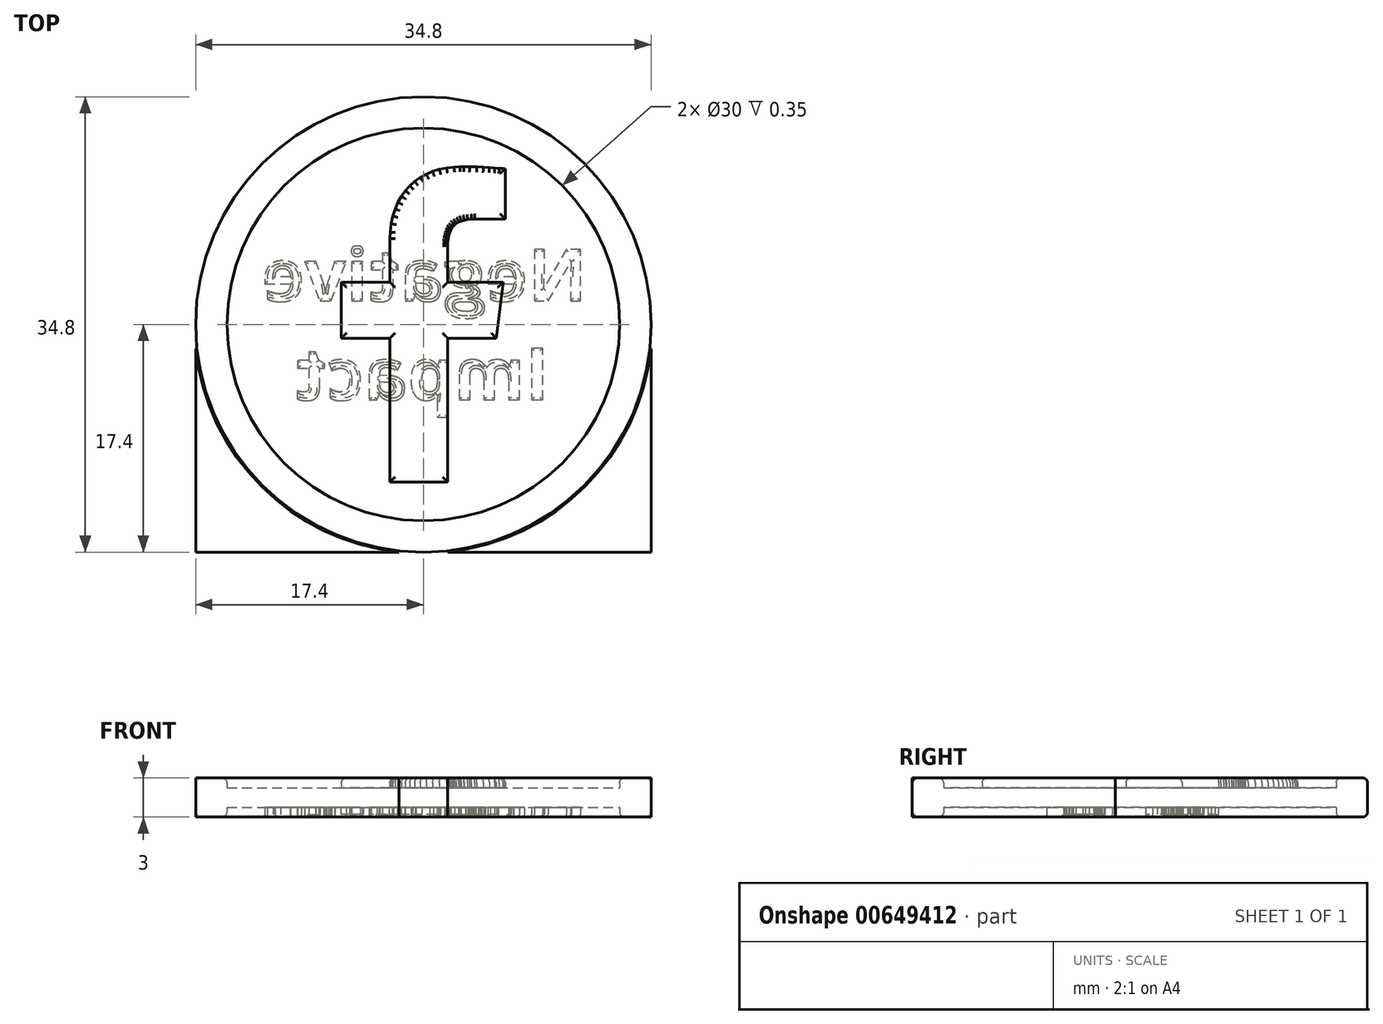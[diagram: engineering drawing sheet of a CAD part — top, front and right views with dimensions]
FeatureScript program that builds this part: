
annotation { "Feature Type Name" : "Feature", "Feature Type Description" : "" }
export const myFeature = defineFeature(function(context is Context, id is Id, definition is map)
    precondition{}
    {
        {
            var Q0;
            Q0=qCreatedBy(makeId("Front.planeOp"),FACE);
            var sketch = newSketch(context, id + "F0", { "sketchPlane" : qUnion([Q0])});
            skLineSegment(sketch, "E0", {"start": v(0, 0) * mm, "end": v(0, 0.75) * mm});
            skLineSegment(sketch, "E1", {"start": v(0, 0.75) * mm, "end": v(-15, 0.75) * mm});
            skLineSegment(sketch, "E2", {"start": v(-15, 0.75) * mm, "end": v(-17.4, 0.75) * mm});
            skLineSegment(sketch, "E3", {"start": v(-17.4, 0.75) * mm, "end": v(-17.4, 0) * mm});
            skLineSegment(sketch, "E4", {"start": v(-17.4, 0) * mm, "end": v(0, 0) * mm});
            skLineSegment(sketch, "E5", {"start": v(-15, 0.75) * mm, "end": v(-15, 0) * mm});
            skLineSegment(sketch, "E6.MirrorCS", {"start": v(0, 0) * mm, "end": v(0, -0.75) * mm});
            skLineSegment(sketch, "E7.MirrorCS", {"start": v(-15, -0.75) * mm, "end": v(-15, 0) * mm});
            skLineSegment(sketch, "E8.MirrorCS", {"start": v(-17.4, -0.75) * mm, "end": v(-17.4, 0) * mm});
            skLineSegment(sketch, "E9.MirrorCS", {"start": v(0, -0.75) * mm, "end": v(-15, -0.75) * mm});
            skLineSegment(sketch, "E10.MirrorCS", {"start": v(-15, -0.75) * mm, "end": v(-17.4, -0.75) * mm});
            skSolve(sketch);
        }
        {
            var Q0;
            {var subQ2=sQuery(id+"F0.wireOp",EDGE,"E7.MirrorCS");Q0=makeQuery(id+"F0.imprint","IMPRINT",FACE,{"disambiguationData":[TD([[makeQuery(id+"F0.imprint","IMPRINT",EDGE,{"derivedFrom":subQ2}),1.0]])]});}
            var Q1;
            Q1=makeQuery(id+"F0.imprint","IMPRINT",FACE,{"disambiguationData":[TD([[makeQuery(id+"F0.imprint","IMPRINT",EDGE,{"derivedFrom":sQuery(id+"F0.wireOp",EDGE,"E2")}),1.0]])]});
            var Q2;
            Q2=sQuery(id+"F0.wireOp",EDGE,"E0");
            revolve(context, id + "F1", {"entities" : qUnion([Q0, Q1]), "axis" : qUnion([Q2]), "revolveType" : RevolveType.FULL});
        }
        {
            var Q0;
            {var subQ0=sQuery(id+"F0.wireOp",EDGE,"E0");Q0=makeQuery(id+"F0.imprint","IMPRINT",FACE,{"disambiguationData":[TD([[makeQuery(id+"F0.imprint","IMPRINT",EDGE,{"derivedFrom":subQ0}),1.0]])]});}
            var Q1;
            {var subQ0=sQuery(id+"F0.wireOp",EDGE,"E6.MirrorCS");Q1=makeQuery(id+"F0.imprint","IMPRINT",FACE,{"disambiguationData":[TD([[makeQuery(id+"F0.imprint","IMPRINT",EDGE,{"derivedFrom":subQ0}),-1.0]])]});}
            var Q2;
            Q2=sQuery(id+"F0.wireOp",EDGE,"E0");
            revolve(context, id + "F2", {"entities" : qUnion([Q0, Q1]), "axis" : qUnion([Q2]), "revolveType" : RevolveType.FULL});
        }
        {
            var Q0;
            Q0=makeQuery(id+"F2.opRevolve","SWEPT_FACE",FACE,{"disambiguationData":[OSD([sQuery(id+"F0.wireOp",EDGE,"E1")])]});
            var sketch = newSketch(context, id + "F3", { "sketchPlane" : qUnion([Q0])});
            skLineSegment(sketch, "E11", {"start": v(1.87, -12.06) * mm, "end": v(1.87, -1.06) * mm});
            skLineSegment(sketch, "E12", {"start": v(1.87, -1.06) * mm, "end": v(5.56, -1.06) * mm});
            skLineSegment(sketch, "E13", {"start": v(5.56, -1.06) * mm, "end": v(6.11, 3.23) * mm});
            skLineSegment(sketch, "E14", {"start": v(6.11, 3.23) * mm, "end": v(1.87, 3.23) * mm});
            skLineSegment(sketch, "E15", {"start": v(1.87, 3.23) * mm, "end": v(1.87, 5.97) * mm});
            skLineSegment(sketch, "E16", {"start": v(1.87, 5.97) * mm, "end": v(1.87, 6.02) * mm});
            skLineSegment(sketch, "E17", {"start": v(1.87, 6.02) * mm, "end": v(1.87, 6.2) * mm});
            skLineSegment(sketch, "E18", {"start": v(1.87, 6.2) * mm, "end": v(1.89, 6.41) * mm});
            skLineSegment(sketch, "E19", {"start": v(1.89, 6.41) * mm, "end": v(1.91, 6.62) * mm});
            skLineSegment(sketch, "E20", {"start": v(1.91, 6.62) * mm, "end": v(1.95, 6.82) * mm});
            skLineSegment(sketch, "E21", {"start": v(1.95, 6.82) * mm, "end": v(2, 7) * mm});
            skLineSegment(sketch, "E22", {"start": v(2, 7) * mm, "end": v(2.07, 7.17) * mm});
            skLineSegment(sketch, "E23", {"start": v(2.07, 7.17) * mm, "end": v(2.16, 7.33) * mm});
            skLineSegment(sketch, "E24", {"start": v(2.16, 7.33) * mm, "end": v(2.26, 7.48) * mm});
            skLineSegment(sketch, "E25", {"start": v(2.26, 7.48) * mm, "end": v(2.39, 7.6) * mm});
            skLineSegment(sketch, "E26", {"start": v(2.39, 7.6) * mm, "end": v(2.54, 7.72) * mm});
            skLineSegment(sketch, "E27", {"start": v(2.54, 7.72) * mm, "end": v(2.71, 7.82) * mm});
            skLineSegment(sketch, "E28", {"start": v(2.71, 7.82) * mm, "end": v(2.9, 7.9) * mm});
            skLineSegment(sketch, "E29", {"start": v(2.9, 7.9) * mm, "end": v(3.13, 7.97) * mm});
            skLineSegment(sketch, "E30", {"start": v(3.13, 7.97) * mm, "end": v(3.39, 8.01) * mm});
            skLineSegment(sketch, "E31", {"start": v(3.39, 8.01) * mm, "end": v(3.67, 8.04) * mm});
            skLineSegment(sketch, "E32", {"start": v(3.67, 8.04) * mm, "end": v(3.91, 8.05) * mm});
            skLineSegment(sketch, "E33", {"start": v(3.91, 8.05) * mm, "end": v(4, 8.05) * mm});
            skLineSegment(sketch, "E34", {"start": v(4, 8.05) * mm, "end": v(6.26, 8.05) * mm});
            skLineSegment(sketch, "E35", {"start": v(6.26, 8.05) * mm, "end": v(6.26, 11.89) * mm});
            skLineSegment(sketch, "E36", {"start": v(6.26, 11.89) * mm, "end": v(6.21, 11.9) * mm});
            skLineSegment(sketch, "E37", {"start": v(6.21, 11.9) * mm, "end": v(6.07, 11.91) * mm});
            skLineSegment(sketch, "E38", {"start": v(6.07, 11.91) * mm, "end": v(5.8, 11.94) * mm});
            skLineSegment(sketch, "E39", {"start": v(5.8, 11.94) * mm, "end": v(5.46, 11.96) * mm});
            skLineSegment(sketch, "E40", {"start": v(5.46, 11.96) * mm, "end": v(5.05, 12) * mm});
            skLineSegment(sketch, "E41", {"start": v(5.05, 12) * mm, "end": v(4.59, 12.02) * mm});
            skLineSegment(sketch, "E42", {"start": v(4.59, 12.02) * mm, "end": v(4.08, 12.04) * mm});
            skLineSegment(sketch, "E43", {"start": v(4.08, 12.04) * mm, "end": v(3.53, 12.05) * mm});
            skLineSegment(sketch, "E44", {"start": v(3.53, 12.05) * mm, "end": v(3.1, 12.06) * mm});
            skLineSegment(sketch, "E45", {"start": v(3.1, 12.06) * mm, "end": v(2.95, 12.06) * mm});
            skLineSegment(sketch, "E46", {"start": v(2.95, 12.06) * mm, "end": v(2.8, 12.06) * mm});
            skLineSegment(sketch, "E47", {"start": v(2.8, 12.06) * mm, "end": v(2.35, 12.03) * mm});
            skLineSegment(sketch, "E48", {"start": v(2.35, 12.03) * mm, "end": v(1.78, 11.96) * mm});
            skLineSegment(sketch, "E49", {"start": v(1.78, 11.96) * mm, "end": v(1.23, 11.85) * mm});
            skLineSegment(sketch, "E50", {"start": v(1.23, 11.85) * mm, "end": v(0.71, 11.69) * mm});
            skLineSegment(sketch, "E51", {"start": v(0.71, 11.69) * mm, "end": v(0.22, 11.48) * mm});
            skLineSegment(sketch, "E52", {"start": v(0.22, 11.48) * mm, "end": v(-0.23, 11.23) * mm});
            skLineSegment(sketch, "E53", {"start": v(-0.23, 11.23) * mm, "end": v(-0.65, 10.94) * mm});
            skLineSegment(sketch, "E54", {"start": v(-0.65, 10.94) * mm, "end": v(-1.03, 10.6) * mm});
            skLineSegment(sketch, "E55", {"start": v(-1.03, 10.6) * mm, "end": v(-1.37, 10.22) * mm});
            skLineSegment(sketch, "E56", {"start": v(-1.37, 10.22) * mm, "end": v(-1.68, 9.8) * mm});
            skLineSegment(sketch, "E57", {"start": v(-1.68, 9.8) * mm, "end": v(-1.94, 9.33) * mm});
            skLineSegment(sketch, "E58", {"start": v(-1.94, 9.33) * mm, "end": v(-2.16, 8.82) * mm});
            skLineSegment(sketch, "E59", {"start": v(-2.16, 8.82) * mm, "end": v(-2.33, 8.28) * mm});
            skLineSegment(sketch, "E60", {"start": v(-2.33, 8.28) * mm, "end": v(-2.46, 7.69) * mm});
            skLineSegment(sketch, "E61", {"start": v(-2.46, 7.69) * mm, "end": v(-2.53, 7.06) * mm});
            skLineSegment(sketch, "E62", {"start": v(-2.53, 7.06) * mm, "end": v(-2.56, 6.56) * mm});
            skLineSegment(sketch, "E63", {"start": v(-2.56, 6.56) * mm, "end": v(-2.56, 6.4) * mm});
            skLineSegment(sketch, "E64", {"start": v(-2.56, 6.4) * mm, "end": v(-2.56, 3.23) * mm});
            skLineSegment(sketch, "E65", {"start": v(-2.56, 3.23) * mm, "end": v(-6.26, 3.23) * mm});
            skLineSegment(sketch, "E66", {"start": v(-6.26, 3.23) * mm, "end": v(-6.26, -1.06) * mm});
            skLineSegment(sketch, "E67", {"start": v(-6.26, -1.06) * mm, "end": v(-2.56, -1.06) * mm});
            skLineSegment(sketch, "E68", {"start": v(-2.56, -1.06) * mm, "end": v(-2.56, -12.06) * mm});
            skLineSegment(sketch, "E69", {"start": v(-2.56, -12.06) * mm, "end": v(1.87, -12.06) * mm});
            skSolve(sketch);
        }
        {
            var Q0;
            Q0=makeQuery(id+"F2.opRevolve","SWEPT_FACE",FACE,{"disambiguationData":[OSD([sQuery(id+"F0.wireOp",EDGE,"E9.MirrorCS")])]});
            var sketch = newSketch(context, id + "F4", { "sketchPlane" : qUnion([Q0])});
            skText(sketch, "E70", { "text": "Negative\n  Impact", "fontName": "OpenSans-Bold.ttf"});
            const initialGuessF4  = {"E70": [0.0125, -0.00178, -1, 0, 0.004]};
            skSetInitialGuess(sketch, initialGuessF4);
            skSolve(sketch);
        }
        {
            var Q0;
            Q0=makeQuery(id+"F3.imprint","IMPRINT",FACE,{"disambiguationData":[TD([[makeQuery(id+"F3.imprint","IMPRINT",EDGE,{"derivedFrom":sQuery(id+"F3.wireOp",EDGE,"E11")}),1.0]])]});
            var Q1;
            Q1=makeQuery(id+"F1.opRevolve","SWEPT_FACE",FACE,{"disambiguationData":[OSD([sQuery(id+"F0.wireOp",EDGE,"E2")])]});
            var Q2;
            Q2=makeQuery(id+"F1.opRevolve","SWEPT_FACE",FACE,{"disambiguationData":[OSD([sQuery(id+"F0.wireOp",EDGE,"E10.MirrorCS")])]});
            var Q3;
            Q3=makeQuery(id+"F4.imprint","IMPRINT",FACE,{"disambiguationData":[TD([[makeQuery(id+"F4.imprint","IMPRINT",EDGE,{"derivedFrom":sQuery(id+"F4.wireOp",EDGE,"e00e6bc2-6b43-4169-90cf-6a860700e017")}),1.0]])]});
            var Q4;
            Q4=makeQuery(id+"F4.imprint","IMPRINT",FACE,{"disambiguationData":[TD([[makeQuery(id+"F4.imprint","IMPRINT",EDGE,{"derivedFrom":sQuery(id+"F4.wireOp",EDGE,"cbd16ef6-c500-4ed5-8440-1c0017b8261a")}),-1.0]])]});
            var Q5;
            Q5=makeQuery(id+"F4.imprint","IMPRINT",FACE,{"disambiguationData":[TD([[makeQuery(id+"F4.imprint","IMPRINT",EDGE,{"derivedFrom":sQuery(id+"F4.wireOp",EDGE,"E70.sketch_text.stroke-34")}),-1.0]])]});
            var Q6;
            Q6=makeQuery(id+"F4.imprint","IMPRINT",FACE,{"disambiguationData":[TD([[makeQuery(id+"F4.imprint","IMPRINT",EDGE,{"derivedFrom":sQuery(id+"F4.wireOp",EDGE,"E70.sketch_text.stroke-14")}),-1.0]])]});
            var Q7;
            Q7=makeQuery(id+"F4.imprint","IMPRINT",FACE,{"disambiguationData":[TD([[makeQuery(id+"F4.imprint","IMPRINT",EDGE,{"derivedFrom":sQuery(id+"F4.wireOp",EDGE,"E70.sketch_text.stroke-0")}),-1.0]])]});
            var Q8;
            Q8=makeQuery(id+"F4.imprint","IMPRINT",FACE,{"disambiguationData":[TD([[makeQuery(id+"F4.imprint","IMPRINT",EDGE,{"derivedFrom":sQuery(id+"F4.wireOp",EDGE,"E70.sketch_text.stroke-160")}),-1.0]])]});
            var Q9;
            Q9=makeQuery(id+"F4.imprint","IMPRINT",FACE,{"disambiguationData":[TD([[makeQuery(id+"F4.imprint","IMPRINT",EDGE,{"derivedFrom":sQuery(id+"F4.wireOp",EDGE,"E70.sketch_text.stroke-164")}),-1.0]])]});
            var Q10;
            Q10=makeQuery(id+"F4.imprint","IMPRINT",FACE,{"disambiguationData":[TD([[makeQuery(id+"F4.imprint","IMPRINT",EDGE,{"derivedFrom":sQuery(id+"F4.wireOp",EDGE,"E70.sketch_text.stroke-192")}),-1.0]])]});
            var Q11;
            Q11=makeQuery(id+"F4.imprint","IMPRINT",FACE,{"disambiguationData":[TD([[makeQuery(id+"F4.imprint","IMPRINT",EDGE,{"derivedFrom":sQuery(id+"F4.wireOp",EDGE,"E70.sketch_text.stroke-215")}),-1.0]])]});
            var Q12;
            Q12=makeQuery(id+"F4.imprint","IMPRINT",FACE,{"disambiguationData":[TD([[makeQuery(id+"F4.imprint","IMPRINT",EDGE,{"derivedFrom":sQuery(id+"F4.wireOp",EDGE,"E70.sketch_text.stroke-240")}),-1.0]])]});
            var Q13;
            Q13=makeQuery(id+"F4.imprint","IMPRINT",FACE,{"disambiguationData":[TD([[makeQuery(id+"F4.imprint","IMPRINT",EDGE,{"derivedFrom":sQuery(id+"F4.wireOp",EDGE,"E70.sketch_text.stroke-254")}),-1.0]])]});
            var Q14;
            Q14=makeQuery(id+"F4.imprint","IMPRINT",FACE,{"disambiguationData":[TD([[makeQuery(id+"F4.imprint","IMPRINT",EDGE,{"derivedFrom":sQuery(id+"F4.wireOp",EDGE,"E70.sketch_text.stroke-78")}),-1.0]])]});
            var Q15;
            Q15=makeQuery(id+"F4.imprint","IMPRINT",FACE,{"disambiguationData":[TD([[makeQuery(id+"F4.imprint","IMPRINT",EDGE,{"derivedFrom":sQuery(id+"F4.wireOp",EDGE,"E70.sketch_text.stroke-103")}),-1.0]])]});
            var Q16;
            Q16=makeQuery(id+"F4.imprint","IMPRINT",FACE,{"disambiguationData":[TD([[makeQuery(id+"F4.imprint","IMPRINT",EDGE,{"derivedFrom":sQuery(id+"F4.wireOp",EDGE,"E70.sketch_text.stroke-126")}),-1.0]])]});
            var Q17;
            Q17=makeQuery(id+"F4.imprint","IMPRINT",FACE,{"disambiguationData":[TD([[makeQuery(id+"F4.imprint","IMPRINT",EDGE,{"derivedFrom":sQuery(id+"F4.wireOp",EDGE,"E70.sketch_text.stroke-121")}),-1.0]])]});
            var Q18;
            Q18=makeQuery(id+"F4.imprint","IMPRINT",FACE,{"disambiguationData":[TD([[makeQuery(id+"F4.imprint","IMPRINT",EDGE,{"derivedFrom":sQuery(id+"F4.wireOp",EDGE,"E70.sketch_text.stroke-130")}),-1.0]])]});
            var Q19;
            Q19=makeQuery(id+"F4.imprint","IMPRINT",FACE,{"disambiguationData":[TD([[makeQuery(id+"F4.imprint","IMPRINT",EDGE,{"derivedFrom":sQuery(id+"F4.wireOp",EDGE,"E70.sketch_text.stroke-140")}),-1.0]])]});
            extrude(context, id + "F5", {"entities" : qUnion([Q0, Q1, Q2, Q3, Q4, Q5, Q6, Q7, Q8, Q9, Q10, Q11, Q12, Q13, Q14, Q15, Q16, Q17, Q18, Q19]), "operationType" : NewBodyOperationType.ADD, "endBound" : BoundingType.SYMMETRIC, "depth" : 1.5 * mm, "offsetDistance" : 25 * mm});
        }
        {
            var Q0;
            Q0=makeQuery(id+"F5.opExtrude","CAP_FACE",FACE,{"disambiguationData":[OSD([sQuery(id+"F0.wireOp",EDGE,"E10.MirrorCS")])],"isStart":true});
            var Q1;
            Q1=makeQuery(id+"F5.opExtrude","CAP_FACE",FACE,{"disambiguationData":[OSD([sQuery(id+"F0.wireOp",EDGE,"E2")])],"isStart":false});
            var Q2;
            Q2=makeQuery(id+"F5.opExtrude","CAP_FACE",FACE,{"disambiguationData":[OSD([sQuery(id+"F4.wireOp",EDGE,"cbd16ef6-c500-4ed5-8440-1c0017b8261a"),sQuery(id+"F4.wireOp",EDGE,"0d944bf3-0ec5-4c38-9916-8d3f37ee8ac4"),sQuery(id+"F4.wireOp",EDGE,"81174dc4-763a-49ac-b099-c01943fa321f"),sQuery(id+"F4.wireOp",EDGE,"576b59ee-5a98-45c4-9437-15f9f7d92798"),sQuery(id+"F4.wireOp",EDGE,"b6bc0b02-f75e-45d8-90bf-1eabf7058279"),sQuery(id+"F4.wireOp",EDGE,"73b536a1-ebc0-4c82-85a4-445a789f644d"),sQuery(id+"F4.wireOp",EDGE,"f7087b31-3228-4bf9-8aa5-93d670d5cce0"),sQuery(id+"F4.wireOp",EDGE,"741630d7-2485-4888-9f90-699ab1dbe6b0"),sQuery(id+"F4.wireOp",EDGE,"e8cdc173-4411-4f79-96bc-056ef1efb820"),sQuery(id+"F4.wireOp",EDGE,"f2d56595-1831-41da-a059-6a4e7aeb48ed"),sQuery(id+"F4.wireOp",EDGE,"39ab4d4d-5ef3-4ee6-bd97-17733d594e21"),sQuery(id+"F4.wireOp",EDGE,"2d56eba7-b366-4cc2-9c15-0fc1e6917ac3"),sQuery(id+"F4.wireOp",EDGE,"xFnOpOKS-PgkY-Xr0f-Dgug-B9nhrKbz7dnA"),sQuery(id+"F4.wireOp",EDGE,"wusehGa3-lIWQ-oOtp-HWoc-AapjoZAoam0S")])],"isStart":true});
            var Q3;
            Q3=makeQuery(id+"F5.opExtrude","CAP_FACE",FACE,{"disambiguationData":[OSD([sQuery(id+"F4.wireOp",EDGE,"e00e6bc2-6b43-4169-90cf-6a860700e017")])],"isStart":true});
            var Q4;
            Q4=makeQuery(id+"F5.opExtrude","CAP_FACE",FACE,{"disambiguationData":[OSD([sQuery(id+"F3.wireOp",EDGE,"E11"),sQuery(id+"F3.wireOp",EDGE,"E12"),sQuery(id+"F3.wireOp",EDGE,"E13"),sQuery(id+"F3.wireOp",EDGE,"E14"),sQuery(id+"F3.wireOp",EDGE,"E15"),sQuery(id+"F3.wireOp",EDGE,"E16"),sQuery(id+"F3.wireOp",EDGE,"E17"),sQuery(id+"F3.wireOp",EDGE,"E18"),sQuery(id+"F3.wireOp",EDGE,"E19"),sQuery(id+"F3.wireOp",EDGE,"E20"),sQuery(id+"F3.wireOp",EDGE,"E21"),sQuery(id+"F3.wireOp",EDGE,"E22"),sQuery(id+"F3.wireOp",EDGE,"E23"),sQuery(id+"F3.wireOp",EDGE,"E24"),sQuery(id+"F3.wireOp",EDGE,"E25"),sQuery(id+"F3.wireOp",EDGE,"E26"),sQuery(id+"F3.wireOp",EDGE,"E27"),sQuery(id+"F3.wireOp",EDGE,"E28"),sQuery(id+"F3.wireOp",EDGE,"E29"),sQuery(id+"F3.wireOp",EDGE,"E30"),sQuery(id+"F3.wireOp",EDGE,"E31"),sQuery(id+"F3.wireOp",EDGE,"E32"),sQuery(id+"F3.wireOp",EDGE,"E33"),sQuery(id+"F3.wireOp",EDGE,"E34"),sQuery(id+"F3.wireOp",EDGE,"E35"),sQuery(id+"F3.wireOp",EDGE,"E36"),sQuery(id+"F3.wireOp",EDGE,"E37"),sQuery(id+"F3.wireOp",EDGE,"E38"),sQuery(id+"F3.wireOp",EDGE,"E39"),sQuery(id+"F3.wireOp",EDGE,"E40"),sQuery(id+"F3.wireOp",EDGE,"E41"),sQuery(id+"F3.wireOp",EDGE,"E42"),sQuery(id+"F3.wireOp",EDGE,"E43"),sQuery(id+"F3.wireOp",EDGE,"E44"),sQuery(id+"F3.wireOp",EDGE,"E45"),sQuery(id+"F3.wireOp",EDGE,"E46"),sQuery(id+"F3.wireOp",EDGE,"E47"),sQuery(id+"F3.wireOp",EDGE,"E48"),sQuery(id+"F3.wireOp",EDGE,"E49"),sQuery(id+"F3.wireOp",EDGE,"E50"),sQuery(id+"F3.wireOp",EDGE,"E51"),sQuery(id+"F3.wireOp",EDGE,"E52"),sQuery(id+"F3.wireOp",EDGE,"E53"),sQuery(id+"F3.wireOp",EDGE,"E54"),sQuery(id+"F3.wireOp",EDGE,"E55"),sQuery(id+"F3.wireOp",EDGE,"E56"),sQuery(id+"F3.wireOp",EDGE,"E57"),sQuery(id+"F3.wireOp",EDGE,"E58"),sQuery(id+"F3.wireOp",EDGE,"E59"),sQuery(id+"F3.wireOp",EDGE,"E60"),sQuery(id+"F3.wireOp",EDGE,"E61"),sQuery(id+"F3.wireOp",EDGE,"E62"),sQuery(id+"F3.wireOp",EDGE,"E63"),sQuery(id+"F3.wireOp",EDGE,"E64"),sQuery(id+"F3.wireOp",EDGE,"E65"),sQuery(id+"F3.wireOp",EDGE,"E66"),sQuery(id+"F3.wireOp",EDGE,"E67"),sQuery(id+"F3.wireOp",EDGE,"E68"),sQuery(id+"F3.wireOp",EDGE,"E69")])],"isStart":false});
            fillet(context, id + "F6", {"entities" : qUnion([Q0, Q1, Q2, Q3, Q4]), "radius" : 0.4 * mm, "tangentPropagation" : true, "allowEdgeOverflow" : false});
        }
        {
            var Q0;
            Q0=makeQuery(id+"F5.opExtrude","CAP_FACE",FACE,{"disambiguationData":[OSD([sQuery(id+"F4.wireOp",EDGE,"E70.sketch_text.stroke-0"),sQuery(id+"F4.wireOp",EDGE,"E70.sketch_text.stroke-1"),sQuery(id+"F4.wireOp",EDGE,"E70.sketch_text.stroke-2"),sQuery(id+"F4.wireOp",EDGE,"E70.sketch_text.stroke-3"),sQuery(id+"F4.wireOp",EDGE,"E70.sketch_text.stroke-4"),sQuery(id+"F4.wireOp",EDGE,"E70.sketch_text.stroke-5"),sQuery(id+"F4.wireOp",EDGE,"E70.sketch_text.stroke-6"),sQuery(id+"F4.wireOp",EDGE,"E70.sketch_text.stroke-7"),sQuery(id+"F4.wireOp",EDGE,"E70.sketch_text.stroke-8"),sQuery(id+"F4.wireOp",EDGE,"E70.sketch_text.stroke-9"),sQuery(id+"F4.wireOp",EDGE,"E70.sketch_text.stroke-10"),sQuery(id+"F4.wireOp",EDGE,"E70.sketch_text.stroke-11"),sQuery(id+"F4.wireOp",EDGE,"E70.sketch_text.stroke-12"),sQuery(id+"F4.wireOp",EDGE,"E70.sketch_text.stroke-13")])],"isStart":true});
            var Q1;
            Q1=makeQuery(id+"F5.opExtrude","CAP_FACE",FACE,{"disambiguationData":[OSD([sQuery(id+"F4.wireOp",EDGE,"E70.sketch_text.stroke-14"),sQuery(id+"F4.wireOp",EDGE,"E70.sketch_text.stroke-15"),sQuery(id+"F4.wireOp",EDGE,"E70.sketch_text.stroke-16"),sQuery(id+"F4.wireOp",EDGE,"E70.sketch_text.stroke-17"),sQuery(id+"F4.wireOp",EDGE,"E70.sketch_text.stroke-18"),sQuery(id+"F4.wireOp",EDGE,"E70.sketch_text.stroke-19"),sQuery(id+"F4.wireOp",EDGE,"E70.sketch_text.stroke-20"),sQuery(id+"F4.wireOp",EDGE,"E70.sketch_text.stroke-21"),sQuery(id+"F4.wireOp",EDGE,"E70.sketch_text.stroke-22"),sQuery(id+"F4.wireOp",EDGE,"E70.sketch_text.stroke-23"),sQuery(id+"F4.wireOp",EDGE,"E70.sketch_text.stroke-24"),sQuery(id+"F4.wireOp",EDGE,"E70.sketch_text.stroke-25"),sQuery(id+"F4.wireOp",EDGE,"E70.sketch_text.stroke-26"),sQuery(id+"F4.wireOp",EDGE,"E70.sketch_text.stroke-27"),sQuery(id+"F4.wireOp",EDGE,"E70.sketch_text.stroke-28"),sQuery(id+"F4.wireOp",EDGE,"E70.sketch_text.stroke-29"),sQuery(id+"F4.wireOp",EDGE,"E70.sketch_text.stroke-30"),sQuery(id+"F4.wireOp",EDGE,"E70.sketch_text.stroke-31"),sQuery(id+"F4.wireOp",EDGE,"E70.sketch_text.stroke-32"),sQuery(id+"F4.wireOp",EDGE,"E70.sketch_text.stroke-33")])],"isStart":true});
            var Q2;
            Q2=makeQuery(id+"F5.opExtrude","CAP_FACE",FACE,{"disambiguationData":[OSD([sQuery(id+"F4.wireOp",EDGE,"E70.sketch_text.stroke-34"),sQuery(id+"F4.wireOp",EDGE,"E70.sketch_text.stroke-35"),sQuery(id+"F4.wireOp",EDGE,"E70.sketch_text.stroke-36"),sQuery(id+"F4.wireOp",EDGE,"E70.sketch_text.stroke-37"),sQuery(id+"F4.wireOp",EDGE,"E70.sketch_text.stroke-38"),sQuery(id+"F4.wireOp",EDGE,"E70.sketch_text.stroke-39"),sQuery(id+"F4.wireOp",EDGE,"E70.sketch_text.stroke-40"),sQuery(id+"F4.wireOp",EDGE,"E70.sketch_text.stroke-41"),sQuery(id+"F4.wireOp",EDGE,"E70.sketch_text.stroke-42"),sQuery(id+"F4.wireOp",EDGE,"E70.sketch_text.stroke-43"),sQuery(id+"F4.wireOp",EDGE,"E70.sketch_text.stroke-44"),sQuery(id+"F4.wireOp",EDGE,"E70.sketch_text.stroke-45"),sQuery(id+"F4.wireOp",EDGE,"E70.sketch_text.stroke-46"),sQuery(id+"F4.wireOp",EDGE,"E70.sketch_text.stroke-47"),sQuery(id+"F4.wireOp",EDGE,"E70.sketch_text.stroke-48"),sQuery(id+"F4.wireOp",EDGE,"E70.sketch_text.stroke-49"),sQuery(id+"F4.wireOp",EDGE,"E70.sketch_text.stroke-50"),sQuery(id+"F4.wireOp",EDGE,"E70.sketch_text.stroke-51"),sQuery(id+"F4.wireOp",EDGE,"E70.sketch_text.stroke-52"),sQuery(id+"F4.wireOp",EDGE,"E70.sketch_text.stroke-53"),sQuery(id+"F4.wireOp",EDGE,"E70.sketch_text.stroke-54"),sQuery(id+"F4.wireOp",EDGE,"E70.sketch_text.stroke-55"),sQuery(id+"F4.wireOp",EDGE,"E70.sketch_text.stroke-56"),sQuery(id+"F4.wireOp",EDGE,"E70.sketch_text.stroke-57"),sQuery(id+"F4.wireOp",EDGE,"E70.sketch_text.stroke-58"),sQuery(id+"F4.wireOp",EDGE,"E70.sketch_text.stroke-59"),sQuery(id+"F4.wireOp",EDGE,"E70.sketch_text.stroke-60"),sQuery(id+"F4.wireOp",EDGE,"E70.sketch_text.stroke-61"),sQuery(id+"F4.wireOp",EDGE,"E70.sketch_text.stroke-62"),sQuery(id+"F4.wireOp",EDGE,"E70.sketch_text.stroke-63"),sQuery(id+"F4.wireOp",EDGE,"E70.sketch_text.stroke-64"),sQuery(id+"F4.wireOp",EDGE,"E70.sketch_text.stroke-65"),sQuery(id+"F4.wireOp",EDGE,"E70.sketch_text.stroke-66"),sQuery(id+"F4.wireOp",EDGE,"E70.sketch_text.stroke-67"),sQuery(id+"F4.wireOp",EDGE,"E70.sketch_text.stroke-68"),sQuery(id+"F4.wireOp",EDGE,"E70.sketch_text.stroke-69"),sQuery(id+"F4.wireOp",EDGE,"E70.sketch_text.stroke-70"),sQuery(id+"F4.wireOp",EDGE,"E70.sketch_text.stroke-71"),sQuery(id+"F4.wireOp",EDGE,"E70.sketch_text.stroke-72"),sQuery(id+"F4.wireOp",EDGE,"E70.sketch_text.stroke-73"),sQuery(id+"F4.wireOp",EDGE,"E70.sketch_text.stroke-74"),sQuery(id+"F4.wireOp",EDGE,"E70.sketch_text.stroke-75"),sQuery(id+"F4.wireOp",EDGE,"E70.sketch_text.stroke-76"),sQuery(id+"F4.wireOp",EDGE,"E70.sketch_text.stroke-77")])],"isStart":true});
            var Q3;
            Q3=makeQuery(id+"F5.opExtrude","CAP_FACE",FACE,{"disambiguationData":[OSD([sQuery(id+"F4.wireOp",EDGE,"E70.sketch_text.stroke-78"),sQuery(id+"F4.wireOp",EDGE,"E70.sketch_text.stroke-79"),sQuery(id+"F4.wireOp",EDGE,"E70.sketch_text.stroke-80"),sQuery(id+"F4.wireOp",EDGE,"E70.sketch_text.stroke-81"),sQuery(id+"F4.wireOp",EDGE,"E70.sketch_text.stroke-82"),sQuery(id+"F4.wireOp",EDGE,"E70.sketch_text.stroke-83"),sQuery(id+"F4.wireOp",EDGE,"E70.sketch_text.stroke-84"),sQuery(id+"F4.wireOp",EDGE,"E70.sketch_text.stroke-85"),sQuery(id+"F4.wireOp",EDGE,"E70.sketch_text.stroke-86"),sQuery(id+"F4.wireOp",EDGE,"E70.sketch_text.stroke-87"),sQuery(id+"F4.wireOp",EDGE,"E70.sketch_text.stroke-88"),sQuery(id+"F4.wireOp",EDGE,"E70.sketch_text.stroke-89"),sQuery(id+"F4.wireOp",EDGE,"E70.sketch_text.stroke-90"),sQuery(id+"F4.wireOp",EDGE,"E70.sketch_text.stroke-91"),sQuery(id+"F4.wireOp",EDGE,"E70.sketch_text.stroke-92"),sQuery(id+"F4.wireOp",EDGE,"E70.sketch_text.stroke-93"),sQuery(id+"F4.wireOp",EDGE,"E70.sketch_text.stroke-94"),sQuery(id+"F4.wireOp",EDGE,"E70.sketch_text.stroke-95"),sQuery(id+"F4.wireOp",EDGE,"E70.sketch_text.stroke-96"),sQuery(id+"F4.wireOp",EDGE,"E70.sketch_text.stroke-97"),sQuery(id+"F4.wireOp",EDGE,"E70.sketch_text.stroke-98"),sQuery(id+"F4.wireOp",EDGE,"E70.sketch_text.stroke-99"),sQuery(id+"F4.wireOp",EDGE,"E70.sketch_text.stroke-100"),sQuery(id+"F4.wireOp",EDGE,"E70.sketch_text.stroke-101"),sQuery(id+"F4.wireOp",EDGE,"E70.sketch_text.stroke-102")])],"isStart":true});
            var Q4;
            Q4=makeQuery(id+"F5.opExtrude","CAP_FACE",FACE,{"disambiguationData":[OSD([sQuery(id+"F4.wireOp",EDGE,"E70.sketch_text.stroke-103"),sQuery(id+"F4.wireOp",EDGE,"E70.sketch_text.stroke-104"),sQuery(id+"F4.wireOp",EDGE,"E70.sketch_text.stroke-105"),sQuery(id+"F4.wireOp",EDGE,"E70.sketch_text.stroke-106"),sQuery(id+"F4.wireOp",EDGE,"E70.sketch_text.stroke-107"),sQuery(id+"F4.wireOp",EDGE,"E70.sketch_text.stroke-108"),sQuery(id+"F4.wireOp",EDGE,"E70.sketch_text.stroke-109"),sQuery(id+"F4.wireOp",EDGE,"E70.sketch_text.stroke-110"),sQuery(id+"F4.wireOp",EDGE,"E70.sketch_text.stroke-111"),sQuery(id+"F4.wireOp",EDGE,"E70.sketch_text.stroke-112"),sQuery(id+"F4.wireOp",EDGE,"E70.sketch_text.stroke-113"),sQuery(id+"F4.wireOp",EDGE,"E70.sketch_text.stroke-114"),sQuery(id+"F4.wireOp",EDGE,"E70.sketch_text.stroke-115"),sQuery(id+"F4.wireOp",EDGE,"E70.sketch_text.stroke-116"),sQuery(id+"F4.wireOp",EDGE,"E70.sketch_text.stroke-117"),sQuery(id+"F4.wireOp",EDGE,"E70.sketch_text.stroke-118"),sQuery(id+"F4.wireOp",EDGE,"E70.sketch_text.stroke-119"),sQuery(id+"F4.wireOp",EDGE,"E70.sketch_text.stroke-120")])],"isStart":true});
            var Q5;
            Q5=makeQuery(id+"F5.opExtrude","CAP_FACE",FACE,{"disambiguationData":[OSD([sQuery(id+"F4.wireOp",EDGE,"E70.sketch_text.stroke-126"),sQuery(id+"F4.wireOp",EDGE,"E70.sketch_text.stroke-127"),sQuery(id+"F4.wireOp",EDGE,"E70.sketch_text.stroke-128"),sQuery(id+"F4.wireOp",EDGE,"E70.sketch_text.stroke-129")])],"isStart":true});
            var Q6;
            Q6=makeQuery(id+"F5.opExtrude","CAP_FACE",FACE,{"disambiguationData":[OSD([sQuery(id+"F4.wireOp",EDGE,"E70.sketch_text.stroke-121"),sQuery(id+"F4.wireOp",EDGE,"E70.sketch_text.stroke-122"),sQuery(id+"F4.wireOp",EDGE,"E70.sketch_text.stroke-123"),sQuery(id+"F4.wireOp",EDGE,"E70.sketch_text.stroke-124"),sQuery(id+"F4.wireOp",EDGE,"E70.sketch_text.stroke-125")])],"isStart":true});
            var Q7;
            Q7=makeQuery(id+"F5.opExtrude","CAP_FACE",FACE,{"disambiguationData":[OSD([sQuery(id+"F4.wireOp",EDGE,"E70.sketch_text.stroke-130"),sQuery(id+"F4.wireOp",EDGE,"E70.sketch_text.stroke-131"),sQuery(id+"F4.wireOp",EDGE,"E70.sketch_text.stroke-132"),sQuery(id+"F4.wireOp",EDGE,"E70.sketch_text.stroke-133"),sQuery(id+"F4.wireOp",EDGE,"E70.sketch_text.stroke-134"),sQuery(id+"F4.wireOp",EDGE,"E70.sketch_text.stroke-135"),sQuery(id+"F4.wireOp",EDGE,"E70.sketch_text.stroke-136"),sQuery(id+"F4.wireOp",EDGE,"E70.sketch_text.stroke-137"),sQuery(id+"F4.wireOp",EDGE,"E70.sketch_text.stroke-138"),sQuery(id+"F4.wireOp",EDGE,"E70.sketch_text.stroke-139")])],"isStart":true});
            var Q8;
            Q8=makeQuery(id+"F5.opExtrude","CAP_FACE",FACE,{"disambiguationData":[OSD([sQuery(id+"F4.wireOp",EDGE,"E70.sketch_text.stroke-140"),sQuery(id+"F4.wireOp",EDGE,"E70.sketch_text.stroke-141"),sQuery(id+"F4.wireOp",EDGE,"E70.sketch_text.stroke-142"),sQuery(id+"F4.wireOp",EDGE,"E70.sketch_text.stroke-143"),sQuery(id+"F4.wireOp",EDGE,"E70.sketch_text.stroke-144"),sQuery(id+"F4.wireOp",EDGE,"E70.sketch_text.stroke-145"),sQuery(id+"F4.wireOp",EDGE,"E70.sketch_text.stroke-146"),sQuery(id+"F4.wireOp",EDGE,"E70.sketch_text.stroke-147"),sQuery(id+"F4.wireOp",EDGE,"E70.sketch_text.stroke-148"),sQuery(id+"F4.wireOp",EDGE,"E70.sketch_text.stroke-149"),sQuery(id+"F4.wireOp",EDGE,"E70.sketch_text.stroke-150"),sQuery(id+"F4.wireOp",EDGE,"E70.sketch_text.stroke-151"),sQuery(id+"F4.wireOp",EDGE,"E70.sketch_text.stroke-152"),sQuery(id+"F4.wireOp",EDGE,"E70.sketch_text.stroke-153"),sQuery(id+"F4.wireOp",EDGE,"E70.sketch_text.stroke-154"),sQuery(id+"F4.wireOp",EDGE,"E70.sketch_text.stroke-155"),sQuery(id+"F4.wireOp",EDGE,"E70.sketch_text.stroke-156"),sQuery(id+"F4.wireOp",EDGE,"E70.sketch_text.stroke-157"),sQuery(id+"F4.wireOp",EDGE,"E70.sketch_text.stroke-158"),sQuery(id+"F4.wireOp",EDGE,"E70.sketch_text.stroke-159")])],"isStart":true});
            var Q9;
            Q9=makeQuery(id+"F5.opExtrude","CAP_FACE",FACE,{"disambiguationData":[OSD([sQuery(id+"F4.wireOp",EDGE,"E70.sketch_text.stroke-160"),sQuery(id+"F4.wireOp",EDGE,"E70.sketch_text.stroke-161"),sQuery(id+"F4.wireOp",EDGE,"E70.sketch_text.stroke-162"),sQuery(id+"F4.wireOp",EDGE,"E70.sketch_text.stroke-163")])],"isStart":true});
            var Q10;
            Q10=makeQuery(id+"F5.opExtrude","CAP_FACE",FACE,{"disambiguationData":[OSD([sQuery(id+"F4.wireOp",EDGE,"E70.sketch_text.stroke-164"),sQuery(id+"F4.wireOp",EDGE,"E70.sketch_text.stroke-165"),sQuery(id+"F4.wireOp",EDGE,"E70.sketch_text.stroke-166"),sQuery(id+"F4.wireOp",EDGE,"E70.sketch_text.stroke-167"),sQuery(id+"F4.wireOp",EDGE,"E70.sketch_text.stroke-168"),sQuery(id+"F4.wireOp",EDGE,"E70.sketch_text.stroke-169"),sQuery(id+"F4.wireOp",EDGE,"E70.sketch_text.stroke-170"),sQuery(id+"F4.wireOp",EDGE,"E70.sketch_text.stroke-171"),sQuery(id+"F4.wireOp",EDGE,"E70.sketch_text.stroke-172"),sQuery(id+"F4.wireOp",EDGE,"E70.sketch_text.stroke-173"),sQuery(id+"F4.wireOp",EDGE,"E70.sketch_text.stroke-174"),sQuery(id+"F4.wireOp",EDGE,"E70.sketch_text.stroke-175"),sQuery(id+"F4.wireOp",EDGE,"E70.sketch_text.stroke-176"),sQuery(id+"F4.wireOp",EDGE,"E70.sketch_text.stroke-177"),sQuery(id+"F4.wireOp",EDGE,"E70.sketch_text.stroke-178"),sQuery(id+"F4.wireOp",EDGE,"E70.sketch_text.stroke-179"),sQuery(id+"F4.wireOp",EDGE,"E70.sketch_text.stroke-180"),sQuery(id+"F4.wireOp",EDGE,"E70.sketch_text.stroke-181"),sQuery(id+"F4.wireOp",EDGE,"E70.sketch_text.stroke-182"),sQuery(id+"F4.wireOp",EDGE,"E70.sketch_text.stroke-183"),sQuery(id+"F4.wireOp",EDGE,"E70.sketch_text.stroke-184"),sQuery(id+"F4.wireOp",EDGE,"E70.sketch_text.stroke-185"),sQuery(id+"F4.wireOp",EDGE,"E70.sketch_text.stroke-186"),sQuery(id+"F4.wireOp",EDGE,"E70.sketch_text.stroke-187"),sQuery(id+"F4.wireOp",EDGE,"E70.sketch_text.stroke-188"),sQuery(id+"F4.wireOp",EDGE,"E70.sketch_text.stroke-189"),sQuery(id+"F4.wireOp",EDGE,"E70.sketch_text.stroke-190"),sQuery(id+"F4.wireOp",EDGE,"E70.sketch_text.stroke-191")])],"isStart":true});
            var Q11;
            Q11=makeQuery(id+"F5.opExtrude","CAP_FACE",FACE,{"disambiguationData":[OSD([sQuery(id+"F4.wireOp",EDGE,"E70.sketch_text.stroke-192"),sQuery(id+"F4.wireOp",EDGE,"E70.sketch_text.stroke-193"),sQuery(id+"F4.wireOp",EDGE,"E70.sketch_text.stroke-194"),sQuery(id+"F4.wireOp",EDGE,"E70.sketch_text.stroke-195"),sQuery(id+"F4.wireOp",EDGE,"E70.sketch_text.stroke-196"),sQuery(id+"F4.wireOp",EDGE,"E70.sketch_text.stroke-197"),sQuery(id+"F4.wireOp",EDGE,"E70.sketch_text.stroke-198"),sQuery(id+"F4.wireOp",EDGE,"E70.sketch_text.stroke-199"),sQuery(id+"F4.wireOp",EDGE,"E70.sketch_text.stroke-200"),sQuery(id+"F4.wireOp",EDGE,"E70.sketch_text.stroke-201"),sQuery(id+"F4.wireOp",EDGE,"E70.sketch_text.stroke-202"),sQuery(id+"F4.wireOp",EDGE,"E70.sketch_text.stroke-203"),sQuery(id+"F4.wireOp",EDGE,"E70.sketch_text.stroke-204"),sQuery(id+"F4.wireOp",EDGE,"E70.sketch_text.stroke-205"),sQuery(id+"F4.wireOp",EDGE,"E70.sketch_text.stroke-206"),sQuery(id+"F4.wireOp",EDGE,"E70.sketch_text.stroke-207"),sQuery(id+"F4.wireOp",EDGE,"E70.sketch_text.stroke-208"),sQuery(id+"F4.wireOp",EDGE,"E70.sketch_text.stroke-209"),sQuery(id+"F4.wireOp",EDGE,"E70.sketch_text.stroke-210"),sQuery(id+"F4.wireOp",EDGE,"E70.sketch_text.stroke-211"),sQuery(id+"F4.wireOp",EDGE,"E70.sketch_text.stroke-212"),sQuery(id+"F4.wireOp",EDGE,"E70.sketch_text.stroke-213"),sQuery(id+"F4.wireOp",EDGE,"E70.sketch_text.stroke-214")])],"isStart":true});
            var Q12;
            Q12=makeQuery(id+"F5.opExtrude","CAP_FACE",FACE,{"disambiguationData":[OSD([sQuery(id+"F4.wireOp",EDGE,"E70.sketch_text.stroke-215"),sQuery(id+"F4.wireOp",EDGE,"E70.sketch_text.stroke-216"),sQuery(id+"F4.wireOp",EDGE,"E70.sketch_text.stroke-217"),sQuery(id+"F4.wireOp",EDGE,"E70.sketch_text.stroke-218"),sQuery(id+"F4.wireOp",EDGE,"E70.sketch_text.stroke-219"),sQuery(id+"F4.wireOp",EDGE,"E70.sketch_text.stroke-220"),sQuery(id+"F4.wireOp",EDGE,"E70.sketch_text.stroke-221"),sQuery(id+"F4.wireOp",EDGE,"E70.sketch_text.stroke-222"),sQuery(id+"F4.wireOp",EDGE,"E70.sketch_text.stroke-223"),sQuery(id+"F4.wireOp",EDGE,"E70.sketch_text.stroke-224"),sQuery(id+"F4.wireOp",EDGE,"E70.sketch_text.stroke-225"),sQuery(id+"F4.wireOp",EDGE,"E70.sketch_text.stroke-226"),sQuery(id+"F4.wireOp",EDGE,"E70.sketch_text.stroke-227"),sQuery(id+"F4.wireOp",EDGE,"E70.sketch_text.stroke-228"),sQuery(id+"F4.wireOp",EDGE,"E70.sketch_text.stroke-229"),sQuery(id+"F4.wireOp",EDGE,"E70.sketch_text.stroke-230"),sQuery(id+"F4.wireOp",EDGE,"E70.sketch_text.stroke-231"),sQuery(id+"F4.wireOp",EDGE,"E70.sketch_text.stroke-232"),sQuery(id+"F4.wireOp",EDGE,"E70.sketch_text.stroke-233"),sQuery(id+"F4.wireOp",EDGE,"E70.sketch_text.stroke-234"),sQuery(id+"F4.wireOp",EDGE,"E70.sketch_text.stroke-235"),sQuery(id+"F4.wireOp",EDGE,"E70.sketch_text.stroke-236"),sQuery(id+"F4.wireOp",EDGE,"E70.sketch_text.stroke-237"),sQuery(id+"F4.wireOp",EDGE,"E70.sketch_text.stroke-238"),sQuery(id+"F4.wireOp",EDGE,"E70.sketch_text.stroke-239")])],"isStart":true});
            var Q13;
            Q13=makeQuery(id+"F5.opExtrude","CAP_FACE",FACE,{"disambiguationData":[OSD([sQuery(id+"F4.wireOp",EDGE,"E70.sketch_text.stroke-240"),sQuery(id+"F4.wireOp",EDGE,"E70.sketch_text.stroke-241"),sQuery(id+"F4.wireOp",EDGE,"E70.sketch_text.stroke-242"),sQuery(id+"F4.wireOp",EDGE,"E70.sketch_text.stroke-243"),sQuery(id+"F4.wireOp",EDGE,"E70.sketch_text.stroke-244"),sQuery(id+"F4.wireOp",EDGE,"E70.sketch_text.stroke-245"),sQuery(id+"F4.wireOp",EDGE,"E70.sketch_text.stroke-246"),sQuery(id+"F4.wireOp",EDGE,"E70.sketch_text.stroke-247"),sQuery(id+"F4.wireOp",EDGE,"E70.sketch_text.stroke-248"),sQuery(id+"F4.wireOp",EDGE,"E70.sketch_text.stroke-249"),sQuery(id+"F4.wireOp",EDGE,"E70.sketch_text.stroke-250"),sQuery(id+"F4.wireOp",EDGE,"E70.sketch_text.stroke-251"),sQuery(id+"F4.wireOp",EDGE,"E70.sketch_text.stroke-252"),sQuery(id+"F4.wireOp",EDGE,"E70.sketch_text.stroke-253")])],"isStart":true});
            var Q14;
            Q14=makeQuery(id+"F5.opExtrude","CAP_FACE",FACE,{"disambiguationData":[OSD([sQuery(id+"F4.wireOp",EDGE,"E70.sketch_text.stroke-254"),sQuery(id+"F4.wireOp",EDGE,"E70.sketch_text.stroke-255"),sQuery(id+"F4.wireOp",EDGE,"E70.sketch_text.stroke-256"),sQuery(id+"F4.wireOp",EDGE,"E70.sketch_text.stroke-257"),sQuery(id+"F4.wireOp",EDGE,"E70.sketch_text.stroke-258"),sQuery(id+"F4.wireOp",EDGE,"E70.sketch_text.stroke-259"),sQuery(id+"F4.wireOp",EDGE,"E70.sketch_text.stroke-260"),sQuery(id+"F4.wireOp",EDGE,"E70.sketch_text.stroke-261"),sQuery(id+"F4.wireOp",EDGE,"E70.sketch_text.stroke-262"),sQuery(id+"F4.wireOp",EDGE,"E70.sketch_text.stroke-263"),sQuery(id+"F4.wireOp",EDGE,"E70.sketch_text.stroke-264"),sQuery(id+"F4.wireOp",EDGE,"E70.sketch_text.stroke-265"),sQuery(id+"F4.wireOp",EDGE,"E70.sketch_text.stroke-266"),sQuery(id+"F4.wireOp",EDGE,"E70.sketch_text.stroke-267"),sQuery(id+"F4.wireOp",EDGE,"E70.sketch_text.stroke-268"),sQuery(id+"F4.wireOp",EDGE,"E70.sketch_text.stroke-269"),sQuery(id+"F4.wireOp",EDGE,"E70.sketch_text.stroke-270"),sQuery(id+"F4.wireOp",EDGE,"E70.sketch_text.stroke-271")])],"isStart":true});
            fillet(context, id + "F7", {"entities" : qUnion([Q0, Q1, Q2, Q3, Q4, Q5, Q6, Q7, Q8, Q9, Q10, Q11, Q12, Q13, Q14]), "radius" : 0.2 * mm, "tangentPropagation" : true, "allowEdgeOverflow" : false});
        }
        {
            var Q0;
            Q0=qCreatedBy(makeId("Top.planeOp"),FACE);
            var sketch = newSketch(context, id + "F8", { "sketchPlane" : qUnion([Q0])});
            skCircle(sketch, "E71.0", {"center": v(0, 0) * mm, "radius": 17.4 * mm});
            skLineSegment(sketch, "E72", {"start": v(-17.4, -1.87) * mm, "end": v(-17.4, -17.4) * mm});
            skLineSegment(sketch, "E73", {"start": v(-17.4, -17.4) * mm, "end": v(-1.87, -17.4) * mm});
            skLineSegment(sketch, "E74", {"start": v(17.4, -17.4) * mm, "end": v(17.4, -1.87) * mm});
            skArc(sketch, "E75", {"start": v(1.87, -17.4) * mm, "mid": v(12.37, -12.37) * mm, "end": v(17.4, -1.87) * mm});
            skLineSegment(sketch, "E76.trimOffspring", {"start": v(1.87, -17.4) * mm, "end": v(17.4, -17.4) * mm});
            skArc(sketch, "E77.trimOffspring", {"start": v(-17.4, -1.87) * mm, "mid": v(-12.37, -12.37) * mm, "end": v(-1.87, -17.4) * mm});
            skSolve(sketch);
        }
        {
            var Q0;
            Q0=makeQuery(id+"F8.imprint","IMPRINT",FACE,{"disambiguationData":[TD([[makeQuery(id+"F8.imprint","IMPRINT",EDGE,{"derivedFrom":sQuery(id+"F8.wireOp",EDGE,"E72")}),1.0]])]});
            var Q1;
            Q1=makeQuery(id+"F8.imprint","IMPRINT",FACE,{"disambiguationData":[TD([[makeQuery(id+"F8.imprint","IMPRINT",EDGE,{"derivedFrom":sQuery(id+"F8.wireOp",EDGE,"E74")}),1.0]])]});
            var Q2;
            Q2=makeQuery(id+"F5.opExtrude","CAP_FACE",FACE,{"disambiguationData":[OSD([sQuery(id+"F0.wireOp",EDGE,"E2")])],"isStart":false});
            var Q3;
            Q3=makeQuery(id+"F5.opExtrude","CAP_FACE",FACE,{"disambiguationData":[OSD([sQuery(id+"F0.wireOp",EDGE,"E10.MirrorCS")])],"isStart":true});
            extrude(context, id + "F9", {"entities" : qUnion([Q0, Q1]), "endBound" : BoundingType.UP_TO_SURFACE, "depth" : 25 * mm, "endBoundEntityFace" : qUnion([Q2]), "offsetDistance" : 25 * mm, "hasSecondDirection" : true, "secondDirectionBound" : SecondDirectionBoundingType.UP_TO_SURFACE, "secondDirectionOppositeDirection" : true, "secondDirectionDepth" : 25 * mm, "secondDirectionBoundEntityFace" : qUnion([Q3])});
        }
    });
